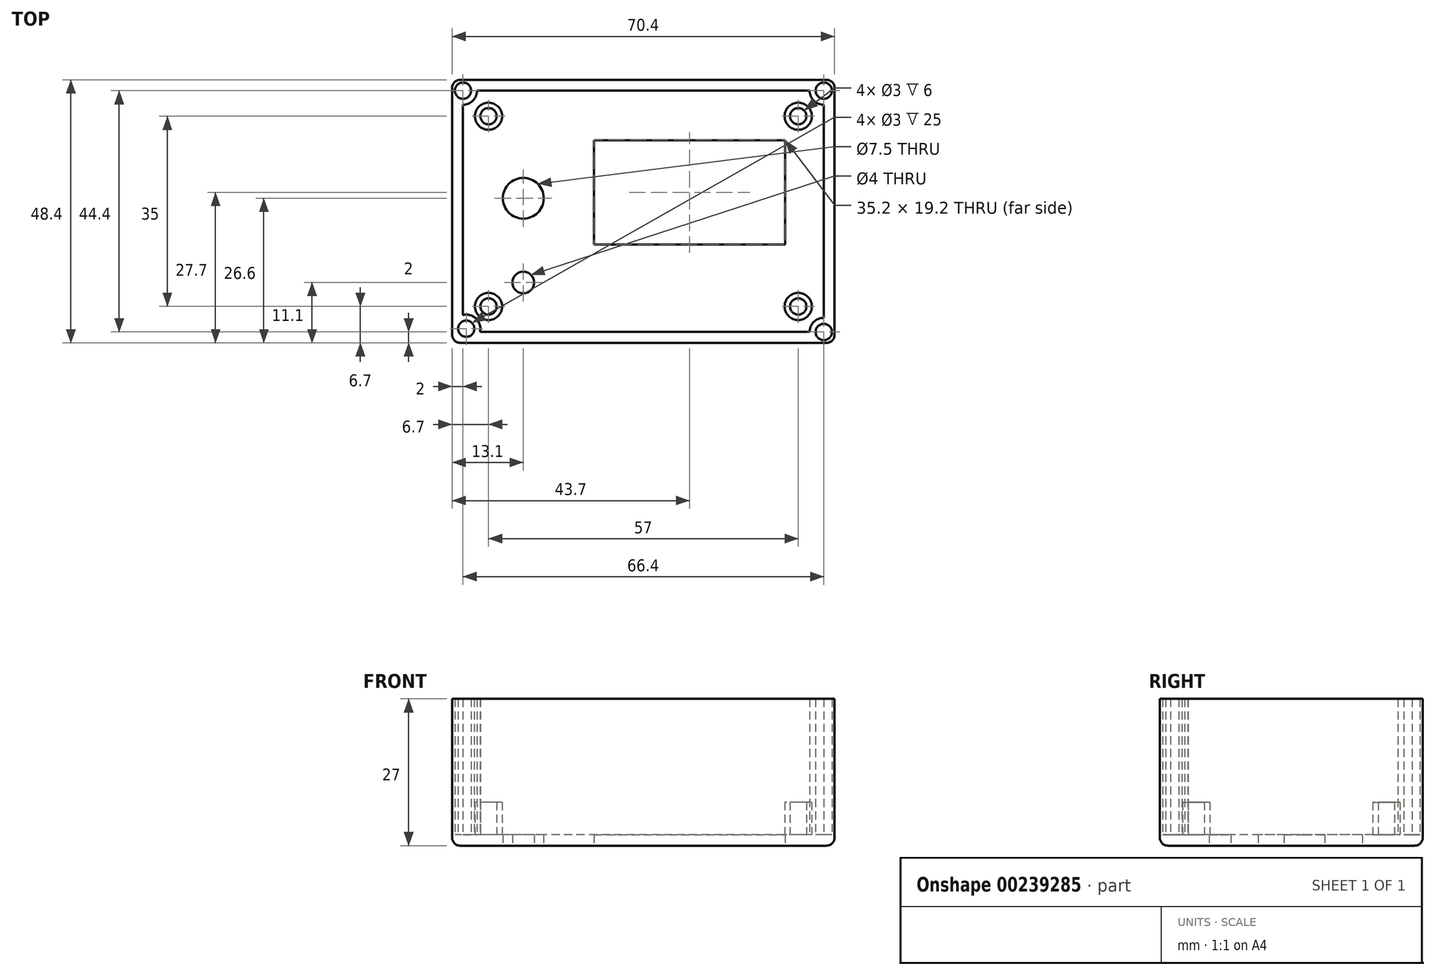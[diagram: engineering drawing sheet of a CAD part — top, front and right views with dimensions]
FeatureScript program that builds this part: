
annotation { "Feature Type Name" : "Feature", "Feature Type Description" : "" }
export const myFeature = defineFeature(function(context is Context, id is Id, definition is map)
    precondition{}
    {
        {
            var Q0;
            Q0=qCreatedBy(makeId("Top.planeOp"),FACE);
            var sketch = newSketch(context, id + "F0", { "sketchPlane" : qUnion([Q0])});
            skPoint(sketch, "E0.middle", {"position": v(0, 0) * mm});
            skLineSegment(sketch, "E1.bottom", {"start": v(35.2, 24.2) * mm, "end": v(-35.2, 24.2) * mm});
            skLineSegment(sketch, "E1.top", {"start": v(35.2, -24.2) * mm, "end": v(-35.2, -24.2) * mm});
            skLineSegment(sketch, "E1.left", {"start": v(35.2, 24.2) * mm, "end": v(35.2, -24.2) * mm});
            skLineSegment(sketch, "E1.right", {"start": v(-35.2, 24.2) * mm, "end": v(-35.2, -24.2) * mm});
            skSolve(sketch);
        }
        {
            var Q0;
            Q0=qCreatedBy(makeId("Top.planeOp"),FACE);
            var sketch = newSketch(context, id + "F1", { "sketchPlane" : qUnion([Q0])});
            skLineSegment(sketch, "E2.bottom", {"start": v(28.5, 17.5) * mm, "end": v(-28.5, 17.5) * mm});
            skLineSegment(sketch, "E2.top", {"start": v(28.5, -17.5) * mm, "end": v(-28.5, -17.5) * mm});
            skLineSegment(sketch, "E2.left", {"start": v(28.5, 17.5) * mm, "end": v(28.5, -17.5) * mm});
            skLineSegment(sketch, "E2.right", {"start": v(-28.5, 17.5) * mm, "end": v(-28.5, -17.5) * mm});
            skPoint(sketch, "E2.middle", {"position": v(0, 0) * mm});
            skLineSegment(sketch, "E3.bottom", {"start": v(35.2, 24.2) * mm, "end": v(-35.2, 24.2) * mm});
            skLineSegment(sketch, "E3.top", {"start": v(35.2, -24.2) * mm, "end": v(-35.2, -24.2) * mm});
            skLineSegment(sketch, "E3.left", {"start": v(35.2, 24.2) * mm, "end": v(35.2, -24.2) * mm});
            skLineSegment(sketch, "E3.right", {"start": v(-35.2, 24.2) * mm, "end": v(-35.2, -24.2) * mm});
            skCircle(sketch, "E4", {"center": v(-28.5, 17.5) * mm, "radius": 2.5 * mm});
            skCircle(sketch, "E5", {"center": v(-28.5, 17.5) * mm, "radius": 1.5 * mm});
            skCircle(sketch, "E6", {"center": v(28.5, 17.5) * mm, "radius": 2.5 * mm});
            skCircle(sketch, "E7", {"center": v(28.5, 17.5) * mm, "radius": 1.5 * mm});
            skCircle(sketch, "E8", {"center": v(28.5, -17.5) * mm, "radius": 2.5 * mm});
            skCircle(sketch, "E9", {"center": v(28.5, -17.5) * mm, "radius": 1.5 * mm});
            skCircle(sketch, "E10", {"center": v(-28.5, -17.5) * mm, "radius": 2.5 * mm});
            skCircle(sketch, "E11", {"center": v(-28.5, -17.5) * mm, "radius": 1.5 * mm});
            skCircle(sketch, "E12", {"center": v(-22.1, 2.4) * mm, "radius": 3.75 * mm});
            skCircle(sketch, "E13", {"center": v(-22.1, -13.1) * mm, "radius": 2 * mm});
            skLineSegment(sketch, "E14.bottom", {"start": v(32, 21) * mm, "end": v(-32, 21) * mm});
            skLineSegment(sketch, "E14.top", {"start": v(32, -21) * mm, "end": v(-32, -21) * mm});
            skLineSegment(sketch, "E14.left", {"start": v(32, 21) * mm, "end": v(32, -21) * mm});
            skLineSegment(sketch, "E14.right", {"start": v(-32, 21) * mm, "end": v(-32, -21) * mm});
            skLineSegment(sketch, "E15.bottom", {"start": v(26.1, -6.1) * mm, "end": v(-9.1, -6.1) * mm});
            skLineSegment(sketch, "E15.top", {"start": v(26.1, 13.1) * mm, "end": v(-9.1, 13.1) * mm});
            skLineSegment(sketch, "E15.left", {"start": v(26.1, -6.1) * mm, "end": v(26.1, 13.1) * mm});
            skLineSegment(sketch, "E15.right", {"start": v(-9.1, -6.1) * mm, "end": v(-9.1, 13.1) * mm});
            skPoint(sketch, "E15.middle", {"position": v(8.5, 3.5) * mm});
            skSolve(sketch);
        }
        {
            var Q0;
            Q0 = qSketchRegion(id + "F0", true);
            extrude(context, id + "F2", {"entities" : qUnion([Q0]), "depth" : 27 * mm});
        }
        {
            var Q0;
            Q0=makeQuery(id+"F2.opExtrude","CAP_FACE",FACE,{"disambiguationData":[OSD([sQuery(id+"F0.wireOp",EDGE,"E1.bottom"),sQuery(id+"F0.wireOp",EDGE,"E1.top"),sQuery(id+"F0.wireOp",EDGE,"E1.left"),sQuery(id+"F0.wireOp",EDGE,"E1.right")])],"isStart":false});
            shell(context, id + "F3", {"entities" : qUnion([Q0]), "thickness" : 2 * mm});
        }
        {
            var Q0;
            Q0=makeQuery(id+"F2.opExtrude","SWEPT_EDGE",EDGE,{"disambiguationData":[OSD([sQuery(id+"F0.wireOp",EDGE,"E1.bottom"),sQuery(id+"F0.wireOp",EDGE,"E1.right")])]});
            var Q1;
            Q1=makeQuery(id+"F2.opExtrude","SWEPT_EDGE",EDGE,{"disambiguationData":[OSD([sQuery(id+"F0.wireOp",EDGE,"E1.top"),sQuery(id+"F0.wireOp",EDGE,"E1.right")])]});
            var Q2;
            Q2=makeQuery(id+"F2.opExtrude","CAP_EDGE",EDGE,{"disambiguationData":[OSD([sQuery(id+"F0.wireOp",EDGE,"E1.right")])],"isStart":true});
            var Q3;
            Q3=makeQuery(id+"F2.opExtrude","CAP_EDGE",EDGE,{"disambiguationData":[OSD([sQuery(id+"F0.wireOp",EDGE,"E1.bottom")])],"isStart":true});
            var Q4;
            Q4=makeQuery(id+"F2.opExtrude","CAP_EDGE",EDGE,{"disambiguationData":[OSD([sQuery(id+"F0.wireOp",EDGE,"E1.top")])],"isStart":true});
            var Q5;
            Q5=makeQuery(id+"F2.opExtrude","CAP_EDGE",EDGE,{"disambiguationData":[OSD([sQuery(id+"F0.wireOp",EDGE,"E1.left")])],"isStart":true});
            var Q6;
            Q6=makeQuery(id+"F2.opExtrude","SWEPT_EDGE",EDGE,{"disambiguationData":[OSD([sQuery(id+"F0.wireOp",EDGE,"E1.top"),sQuery(id+"F0.wireOp",EDGE,"E1.left")])]});
            var Q7;
            Q7=makeQuery(id+"F2.opExtrude","SWEPT_EDGE",EDGE,{"disambiguationData":[OSD([sQuery(id+"F0.wireOp",EDGE,"E1.bottom"),sQuery(id+"F0.wireOp",EDGE,"E1.left")])]});
            fillet(context, id + "F4", {"entities" : qUnion([Q0, Q1, Q2, Q3, Q4, Q5, Q6, Q7]), "radius" : 1.5 * mm, "tangentPropagation" : true, "allowEdgeOverflow" : false});
        }
        {
            var Q0;
            Q0=makeQuery(id+"F1.imprint","IMPRINT",FACE,{"disambiguationData":[TD([[makeQuery(id+"F1.imprint","IMPRINT",EDGE,{"derivedFrom":sQuery(id+"F1.wireOp",EDGE,"E13")}),1.0]])]});
            var Q1;
            Q1=makeQuery(id+"F1.imprint","IMPRINT",FACE,{"disambiguationData":[TD([[makeQuery(id+"F1.imprint","IMPRINT",EDGE,{"derivedFrom":sQuery(id+"F1.wireOp",EDGE,"E12")}),1.0]])]});
            extrude(context, id + "F5", {"entities" : qUnion([Q0, Q1]), "operationType" : NewBodyOperationType.REMOVE, "depth" : 25 * mm});
        }
        {
            var Q0;
            {var subQ0=sQuery(id+"F1.wireOp",EDGE,"E7");var subQ1=sQuery(id+"F1.wireOp",EDGE,"E2.bottom");var subQ2=makeQuery(id+"F1.imprint","INTERSECT",VERTEX,{"derivedFrom":[subQ1,subQ0]});Q0=makeQuery(id+"F1.imprint","IMPRINT",FACE,{"disambiguationData":[TD([[makeQuery(id+"F1.imprint","IMPRINT",EDGE,{"disambiguationData":[TD([[subQ2,-1.0]])],"derivedFrom":subQ1}),1.0]])]});}
            var Q1;
            {var subQ0=sQuery(id+"F1.wireOp",EDGE,"E7");var subQ1=sQuery(id+"F1.wireOp",EDGE,"E2.bottom");var subQ2=makeQuery(id+"F1.imprint","INTERSECT",VERTEX,{"derivedFrom":[subQ1,subQ0]});Q1=makeQuery(id+"F1.imprint","IMPRINT",FACE,{"disambiguationData":[TD([[makeQuery(id+"F1.imprint","IMPRINT",EDGE,{"disambiguationData":[TD([[subQ2,-1.0]])],"derivedFrom":subQ1}),-1.0]])]});}
            var Q2;
            {var subQ0=sQuery(id+"F1.wireOp",EDGE,"E9");var subQ1=sQuery(id+"F1.wireOp",EDGE,"E2.top");var subQ2=makeQuery(id+"F1.imprint","INTERSECT",VERTEX,{"derivedFrom":[subQ1,subQ0]});Q2=makeQuery(id+"F1.imprint","IMPRINT",FACE,{"disambiguationData":[TD([[makeQuery(id+"F1.imprint","IMPRINT",EDGE,{"disambiguationData":[TD([[subQ2,-1.0]])],"derivedFrom":subQ1}),-1.0]])]});}
            var Q3;
            {var subQ0=sQuery(id+"F1.wireOp",EDGE,"E9");var subQ1=sQuery(id+"F1.wireOp",EDGE,"E2.top");var subQ2=makeQuery(id+"F1.imprint","INTERSECT",VERTEX,{"derivedFrom":[subQ1,subQ0]});Q3=makeQuery(id+"F1.imprint","IMPRINT",FACE,{"disambiguationData":[TD([[makeQuery(id+"F1.imprint","IMPRINT",EDGE,{"disambiguationData":[TD([[subQ2,-1.0]])],"derivedFrom":subQ1}),1.0]])]});}
            var Q4;
            {var subQ0=sQuery(id+"F1.wireOp",EDGE,"E10");var subQ1=sQuery(id+"F1.wireOp",EDGE,"E2.top");var subQ2=makeQuery(id+"F1.imprint","INTERSECT",VERTEX,{"derivedFrom":[subQ1,subQ0]});Q4=makeQuery(id+"F1.imprint","IMPRINT",FACE,{"disambiguationData":[TD([[makeQuery(id+"F1.imprint","IMPRINT",EDGE,{"disambiguationData":[TD([[subQ2,-1.0]])],"derivedFrom":subQ1}),1.0]])]});}
            var Q5;
            {var subQ0=sQuery(id+"F1.wireOp",EDGE,"E10");var subQ1=sQuery(id+"F1.wireOp",EDGE,"E2.top");var subQ2=makeQuery(id+"F1.imprint","INTERSECT",VERTEX,{"derivedFrom":[subQ1,subQ0]});Q5=makeQuery(id+"F1.imprint","IMPRINT",FACE,{"disambiguationData":[TD([[makeQuery(id+"F1.imprint","IMPRINT",EDGE,{"disambiguationData":[TD([[subQ2,-1.0]])],"derivedFrom":subQ1}),-1.0]])]});}
            var Q6;
            {var subQ0=sQuery(id+"F1.wireOp",EDGE,"E4");var subQ1=sQuery(id+"F1.wireOp",EDGE,"E2.bottom");var subQ2=makeQuery(id+"F1.imprint","INTERSECT",VERTEX,{"derivedFrom":[subQ1,subQ0]});Q6=makeQuery(id+"F1.imprint","IMPRINT",FACE,{"disambiguationData":[TD([[makeQuery(id+"F1.imprint","IMPRINT",EDGE,{"disambiguationData":[TD([[subQ2,-1.0]])],"derivedFrom":subQ1}),-1.0]])]});}
            var Q7;
            {var subQ0=sQuery(id+"F1.wireOp",EDGE,"E4");var subQ1=sQuery(id+"F1.wireOp",EDGE,"E2.bottom");var subQ2=makeQuery(id+"F1.imprint","INTERSECT",VERTEX,{"derivedFrom":[subQ1,subQ0]});Q7=makeQuery(id+"F1.imprint","IMPRINT",FACE,{"disambiguationData":[TD([[makeQuery(id+"F1.imprint","IMPRINT",EDGE,{"disambiguationData":[TD([[subQ2,-1.0]])],"derivedFrom":subQ1}),1.0]])]});}
            extrude(context, id + "F6", {"entities" : qUnion([Q0, Q1, Q2, Q3, Q4, Q5, Q6, Q7]), "operationType" : NewBodyOperationType.ADD, "depth" : 8 * mm});
        }
        {
            var Q0;
            Q0=makeQuery(id+"F1.imprint","IMPRINT",FACE,{"disambiguationData":[TD([[makeQuery(id+"F1.imprint","IMPRINT",EDGE,{"derivedFrom":sQuery(id+"F1.wireOp",EDGE,"E15.bottom")}),-1.0]])]});
            extrude(context, id + "F7", {"entities" : qUnion([Q0]), "operationType" : NewBodyOperationType.REMOVE, "depth" : 25 * mm});
        }
        {
            var Q0;
            {var subQ0=sQuery(id+"F0.wireOp",EDGE,"E1.right");var subQ1=sQuery(id+"F0.wireOp",EDGE,"E1.left");var subQ2=sQuery(id+"F0.wireOp",EDGE,"E1.top");var subQ3=sQuery(id+"F0.wireOp",EDGE,"E1.bottom");Q0=makeQuery(id+"F6.boolean.opBoolean","SPLIT",FACE,{"disambiguationData":[TD([makeQuery(id+"F3.opShell","OFFSET_FACE",FACE,{"disambiguationData":[OSD([subQ3])]})])],"derivedFrom":makeQuery(id+"F3.opShell","OFFSET_FACE",FACE,{"disambiguationData":[OSD([subQ3,subQ2,subQ1,subQ0])]})});}
            var sketch = newSketch(context, id + "F8", { "sketchPlane" : qUnion([Q0])});
            skCircle(sketch, "E16", {"center": v(33.2, 22.2) * mm, "radius": 2.6 * mm});
            skCircle(sketch, "E17", {"center": v(33.2, 22.2) * mm, "radius": 1.5 * mm});
            skCircle(sketch, "E18", {"center": v(33.2, -22.2) * mm, "radius": 2.6 * mm});
            skCircle(sketch, "E19", {"center": v(33.2, -22.2) * mm, "radius": 1.5 * mm});
            skCircle(sketch, "E20", {"center": v(-33.2, 22.2) * mm, "radius": 2.6 * mm});
            skCircle(sketch, "E21", {"center": v(-33.2, 22.2) * mm, "radius": 1.5 * mm});
            skPoint(sketch, "E22", {"position": v(-32.6, -21.6) * mm});
            skCircle(sketch, "E23", {"center": v(-32.6, -21.6) * mm, "radius": 1.5 * mm});
            skCircle(sketch, "E24", {"center": v(-32.6, -21.6) * mm, "radius": 2.6 * mm});
            skSolve(sketch);
        }
        {
            var Q0;
            {var subQ0=sQuery(id+"F8.wireOp",EDGE,"E20");var subQ1=sQuery(id+"F0.wireOp",EDGE,"E1.bottom");var subQ2=makeQuery(id+"F3.opShell","OFFSET_EDGE",EDGE,{"disambiguationData":[OSD([subQ1]),TDD([makeQuery(id+"F2.opExtrude","CAP_EDGE",EDGE,{"disambiguationData":[OSD([subQ1])],"isStart":true})])]});var subQ3=makeQuery(id+"F8.imprint","INTERSECT",VERTEX,{"derivedFrom":[subQ2,subQ0]});Q0=makeQuery(id+"F8.imprint","IMPRINT",FACE,{"disambiguationData":[TD([[makeQuery(id+"F8.imprint","IMPRINT",EDGE,{"disambiguationData":[TD([[subQ3,1.0]])],"derivedFrom":subQ0}),1.0]])]});}
            var Q1;
            {var subQ0=sQuery(id+"F8.wireOp",EDGE,"nzfbPZwC-VuTe-jmoL-FVRn-kgNciz9S2pEG");var subQ1=sQuery(id+"F0.wireOp",EDGE,"E1.top");var subQ2=makeQuery(id+"F3.opShell","OFFSET_EDGE",EDGE,{"disambiguationData":[OSD([subQ1]),TDD([makeQuery(id+"F2.opExtrude","CAP_EDGE",EDGE,{"disambiguationData":[OSD([subQ1])],"isStart":true})])]});var subQ3=makeQuery(id+"F8.imprint","INTERSECT",VERTEX,{"derivedFrom":[subQ2,subQ0]});Q1=makeQuery(id+"F8.imprint","IMPRINT",FACE,{"disambiguationData":[TD([[makeQuery(id+"F8.imprint","IMPRINT",EDGE,{"disambiguationData":[TD([[subQ3,-1.0]])],"derivedFrom":subQ0}),1.0]])]});}
            var Q2;
            {var subQ0=sQuery(id+"F8.wireOp",EDGE,"E16");var subQ1=sQuery(id+"F0.wireOp",EDGE,"E1.bottom");var subQ2=makeQuery(id+"F3.opShell","OFFSET_EDGE",EDGE,{"disambiguationData":[OSD([subQ1]),TDD([makeQuery(id+"F2.opExtrude","CAP_EDGE",EDGE,{"disambiguationData":[OSD([subQ1])],"isStart":true})])]});var subQ3=makeQuery(id+"F8.imprint","INTERSECT",VERTEX,{"derivedFrom":[subQ2,subQ0]});Q2=makeQuery(id+"F8.imprint","IMPRINT",FACE,{"disambiguationData":[TD([[makeQuery(id+"F8.imprint","IMPRINT",EDGE,{"disambiguationData":[TD([[subQ3,-1.0]])],"derivedFrom":subQ0}),1.0]])]});}
            var Q3;
            {var subQ0=sQuery(id+"F8.wireOp",EDGE,"E18");var subQ1=sQuery(id+"F0.wireOp",EDGE,"E1.top");var subQ2=makeQuery(id+"F3.opShell","OFFSET_EDGE",EDGE,{"disambiguationData":[OSD([subQ1]),TDD([makeQuery(id+"F2.opExtrude","CAP_EDGE",EDGE,{"disambiguationData":[OSD([subQ1])],"isStart":true})])]});var subQ3=makeQuery(id+"F8.imprint","INTERSECT",VERTEX,{"derivedFrom":[subQ2,subQ0]});Q3=makeQuery(id+"F8.imprint","IMPRINT",FACE,{"disambiguationData":[TD([[makeQuery(id+"F8.imprint","IMPRINT",EDGE,{"disambiguationData":[TD([[subQ3,1.0]])],"derivedFrom":subQ0}),1.0]])]});}
            var Q4;
            {var subQ0=sQuery(id+"F8.wireOp",EDGE,"E23");var subQ1=sQuery(id+"F0.wireOp",EDGE,"E1.top");var subQ2=makeQuery(id+"F3.opShell","OFFSET_EDGE",EDGE,{"disambiguationData":[OSD([subQ1]),TDD([makeQuery(id+"F2.opExtrude","CAP_EDGE",EDGE,{"disambiguationData":[OSD([subQ1])],"isStart":true})])]});var subQ3=makeQuery(id+"F8.imprint","INTERSECT",VERTEX,{"derivedFrom":[subQ2,subQ0]});Q4=makeQuery(id+"F8.imprint","IMPRINT",FACE,{"disambiguationData":[TD([[makeQuery(id+"F8.imprint","IMPRINT",EDGE,{"disambiguationData":[TD([[subQ3,-1.0]])],"derivedFrom":subQ0}),-1.0]])]});}
            extrude(context, id + "F9", {"entities" : qUnion([Q0, Q1, Q2, Q3, Q4]), "operationType" : NewBodyOperationType.ADD, "depth" : 25 * mm});
        }
        {
            var Q0;
            {var subQ0=sQuery(id+"F0.wireOp",EDGE,"E1.right");var subQ1=sQuery(id+"F0.wireOp",EDGE,"E1.bottom");var subQ2=sQuery(id+"F0.wireOp",EDGE,"E1.top");var subQ3=sQuery(id+"F0.wireOp",EDGE,"E1.left");Q0=makeQuery(id+"F9.boolean.opBoolean","MERGE",FACE,{"derivedFrom":[makeQuery(id+"F2.opExtrude","CAP_FACE",FACE,{"disambiguationData":[OSD([subQ1,subQ2,subQ3,subQ0])],"isStart":false}),makeQuery(id+"F9.opExtrude","CAP_FACE",FACE,{"disambiguationData":[OSD([subQ1,subQ3,sQuery(id+"F8.wireOp",EDGE,"E16"),sQuery(id+"F8.wireOp",EDGE,"E17")])],"isStart":false}),makeQuery(id+"F9.opExtrude","CAP_FACE",FACE,{"disambiguationData":[OSD([subQ2,subQ3,sQuery(id+"F8.wireOp",EDGE,"E18"),sQuery(id+"F8.wireOp",EDGE,"E19")])],"isStart":false}),makeQuery(id+"F9.opExtrude","CAP_FACE",FACE,{"disambiguationData":[OSD([subQ2,subQ0,sQuery(id+"F8.wireOp",EDGE,"nzfbPZwC-VuTe-jmoL-FVRn-kgNciz9S2pEG"),sQuery(id+"F8.wireOp",EDGE,"dHVGQzkf-PjCo-ogIC-HjeQ-oKPRlGA4aPXv")])],"isStart":false}),makeQuery(id+"F9.opExtrude","CAP_FACE",FACE,{"disambiguationData":[OSD([subQ1,subQ0,sQuery(id+"F8.wireOp",EDGE,"E20"),sQuery(id+"F8.wireOp",EDGE,"E21")])],"isStart":false})]});}
            var sketch = newSketch(context, id + "F10", { "sketchPlane" : qUnion([Q0])});
            skCircle(sketch, "E25", {"center": v(-33.2, 22.2) * mm, "radius": 1.5 * mm});
            skCircle(sketch, "E26", {"center": v(33.2, 22.2) * mm, "radius": 1.5 * mm});
            skCircle(sketch, "E27", {"center": v(33.2, -22.2) * mm, "radius": 1.5 * mm});
            skPoint(sketch, "E28", {"position": v(-32.6, -21.6) * mm});
            skCircle(sketch, "E29", {"center": v(-32.6, -21.6) * mm, "radius": 1.5 * mm});
            skSolve(sketch);
        }
        {
            var Q0;
            {var subQ2=sQuery(id+"F0.wireOp",EDGE,"E1.bottom");var subQ4=sQuery(id+"F0.wireOp",EDGE,"E1.right");var subQ7=makeQuery(id+"F3.opShell","OFFSET_FACE",FACE,{"disambiguationData":[OSD([subQ4])]});var subQ14=makeQuery(id+"F9.boolean.opBoolean","SPLIT",EDGE,{"disambiguationData":[TD([subQ7])],"derivedFrom":makeQuery(id+"F3.opShell","OFFSET_EDGE",EDGE,{"disambiguationData":[OSD([subQ2]),TDD([makeQuery(id+"F2.opExtrude","CAP_EDGE",EDGE,{"disambiguationData":[OSD([subQ2])],"isStart":false})])]})});Q0=makeQuery(id+"F10.imprint","IMPRINT",FACE,{"disambiguationData":[TD([[makeQuery(id+"F10.imprint","IMPRINT",EDGE,{"derivedFrom":subQ14}),-1.0]])]});}
            var Q1;
            {var subQ2=sQuery(id+"F0.wireOp",EDGE,"E1.left");var subQ3=sQuery(id+"F0.wireOp",EDGE,"E1.bottom");var subQ8=makeQuery(id+"F3.opShell","OFFSET_FACE",FACE,{"disambiguationData":[OSD([subQ2])]});var subQ14=makeQuery(id+"F9.boolean.opBoolean","SPLIT",EDGE,{"disambiguationData":[TD([subQ8])],"derivedFrom":makeQuery(id+"F3.opShell","OFFSET_EDGE",EDGE,{"disambiguationData":[OSD([subQ3]),TDD([makeQuery(id+"F2.opExtrude","CAP_EDGE",EDGE,{"disambiguationData":[OSD([subQ3])],"isStart":false})])]})});Q1=makeQuery(id+"F10.imprint","IMPRINT",FACE,{"disambiguationData":[TD([[makeQuery(id+"F10.imprint","IMPRINT",EDGE,{"derivedFrom":subQ14}),-1.0]])]});}
            var Q2;
            {var subQ1=sQuery(id+"F0.wireOp",EDGE,"E1.left");var subQ5=sQuery(id+"F0.wireOp",EDGE,"E1.top");var subQ7=makeQuery(id+"F3.opShell","OFFSET_FACE",FACE,{"disambiguationData":[OSD([subQ1])]});var subQ14=makeQuery(id+"F9.boolean.opBoolean","SPLIT",EDGE,{"disambiguationData":[TD([subQ7])],"derivedFrom":makeQuery(id+"F3.opShell","OFFSET_EDGE",EDGE,{"disambiguationData":[OSD([subQ5]),TDD([makeQuery(id+"F2.opExtrude","CAP_EDGE",EDGE,{"disambiguationData":[OSD([subQ5])],"isStart":false})])]})});Q2=makeQuery(id+"F10.imprint","IMPRINT",FACE,{"disambiguationData":[TD([[makeQuery(id+"F10.imprint","IMPRINT",EDGE,{"derivedFrom":subQ14}),1.0]])]});}
            var Q3;
            {var subQ4=sQuery(id+"F0.wireOp",EDGE,"E1.right");var subQ5=sQuery(id+"F0.wireOp",EDGE,"E1.top");var subQ7=makeQuery(id+"F3.opShell","OFFSET_FACE",FACE,{"disambiguationData":[OSD([subQ4])]});var subQ14=makeQuery(id+"F9.boolean.opBoolean","SPLIT",EDGE,{"disambiguationData":[TD([subQ7])],"derivedFrom":makeQuery(id+"F3.opShell","OFFSET_EDGE",EDGE,{"disambiguationData":[OSD([subQ5]),TDD([makeQuery(id+"F2.opExtrude","CAP_EDGE",EDGE,{"disambiguationData":[OSD([subQ5])],"isStart":false})])]})});Q3=makeQuery(id+"F10.imprint","IMPRINT",FACE,{"disambiguationData":[TD([[makeQuery(id+"F10.imprint","IMPRINT",EDGE,{"derivedFrom":subQ14}),1.0]])]});}
            extrude(context, id + "F11", {"entities" : qUnion([Q0, Q1, Q2, Q3]), "operationType" : NewBodyOperationType.REMOVE, "oppositeDirection" : true, "depth" : 25 * mm});
        }
    });
